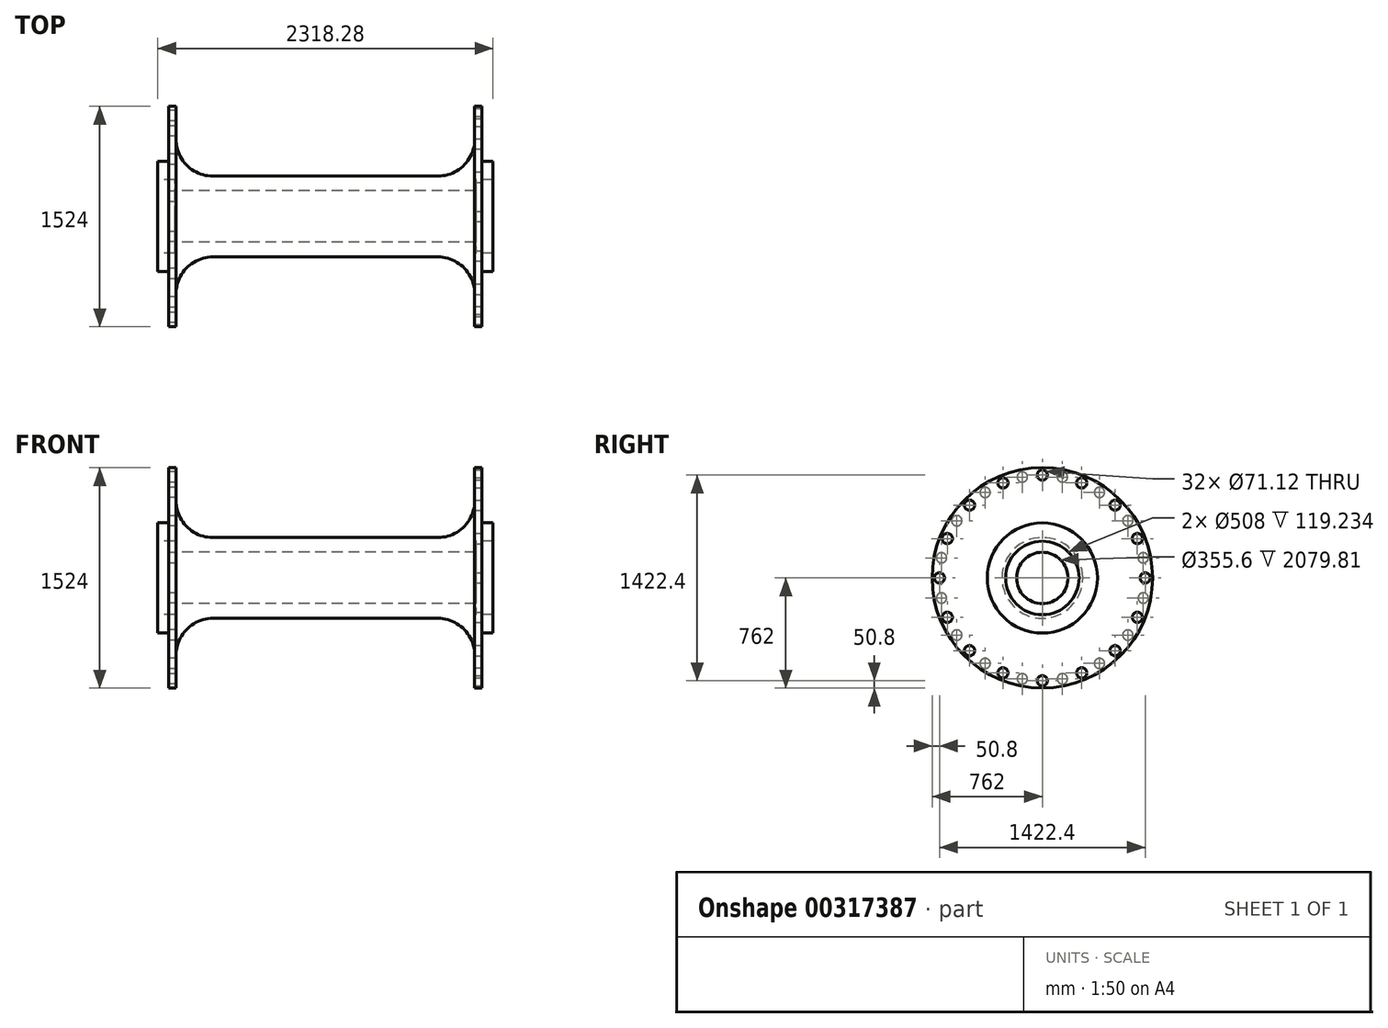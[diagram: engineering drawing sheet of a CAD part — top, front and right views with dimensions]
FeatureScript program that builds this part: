
annotation { "Feature Type Name" : "Feature", "Feature Type Description" : "" }
export const myFeature = defineFeature(function(context is Context, id is Id, definition is map)
    precondition{}
    {
        {
            var Q0;
            Q0=qCreatedBy(makeId("Front.planeOp"),FACE);
            var sketch = newSketch(context, id + "F0", { "sketchPlane" : qUnion([Q0])});
            skLineSegment(sketch, "E0", {"start": v(-1159.14, 0) * mm, "end": v(1380.86, 0) * mm});
            skLineSegment(sketch, "E1", {"start": v(-1159.14, 254) * mm, "end": v(-1039.9, 254) * mm});
            skLineSegment(sketch, "E2", {"start": v(-1039.9, 254) * mm, "end": v(-1039.9, 177.8) * mm});
            skLineSegment(sketch, "E3", {"start": v(-1039.9, 177.8) * mm, "end": v(0, 177.8) * mm});
            skLineSegment(sketch, "E4", {"start": v(0, 177.8) * mm, "end": v(0, 0) * mm});
            skLineSegment(sketch, "E5", {"start": v(-1159.14, 254) * mm, "end": v(-1159.14, 381) * mm});
            skLineSegment(sketch, "E6", {"start": v(-1159.14, 381) * mm, "end": v(-1082.94, 381) * mm});
            skLineSegment(sketch, "E7", {"start": v(-1082.94, 381) * mm, "end": v(-1082.94, 762) * mm});
            skLineSegment(sketch, "E8", {"start": v(-1082.94, 762) * mm, "end": v(-1032.14, 762) * mm});
            skLineSegment(sketch, "E9", {"start": v(-1032.14, 762) * mm, "end": v(-1032.14, 533.4) * mm});
            skLineSegment(sketch, "E10", {"start": v(0, 279.4) * mm, "end": v(-778.14, 279.4) * mm});
            skPoint(sketch, "E11.visualSharp", {"position": v(-1032.14, 279.4) * mm});
            skArc(sketch, "E11.filletArc", {"start": v(-1032.14, 533.4) * mm, "mid": v(-957.75, 353.8) * mm, "end": v(-778.14, 279.4) * mm});
            skLineSegment(sketch, "E12.MirrorCS", {"start": v(1159.14, 254) * mm, "end": v(1039.9, 254) * mm});
            skPoint(sketch, "E13.MirrorP", {"position": v(1032.14, 279.4) * mm});
            skLineSegment(sketch, "E14.MirrorCS", {"start": v(1039.9, 254) * mm, "end": v(1039.9, 177.8) * mm});
            skArc(sketch, "E15.MirrorCS", {"start": v(1032.14, 533.4) * mm, "mid": v(957.75, 353.8) * mm, "end": v(778.14, 279.4) * mm});
            skLineSegment(sketch, "E16.MirrorCS", {"start": v(1039.9, 177.8) * mm, "end": v(0, 177.8) * mm});
            skLineSegment(sketch, "E17.MirrorCS", {"start": v(0, 279.4) * mm, "end": v(778.14, 279.4) * mm});
            skLineSegment(sketch, "E18.MirrorCS", {"start": v(1082.94, 381) * mm, "end": v(1082.94, 762) * mm});
            skLineSegment(sketch, "E19.MirrorCS", {"start": v(1159.14, 381) * mm, "end": v(1082.94, 381) * mm});
            skLineSegment(sketch, "E20.MirrorCS", {"start": v(1082.94, 762) * mm, "end": v(1032.14, 762) * mm});
            skLineSegment(sketch, "E21.MirrorCS", {"start": v(1159.14, 254) * mm, "end": v(1159.14, 381) * mm});
            skLineSegment(sketch, "E22.MirrorCS", {"start": v(1032.14, 762) * mm, "end": v(1032.14, 533.4) * mm});
            skSolve(sketch);
        }
        {
            var Q0;
            Q0=makeQuery(id+"F0.imprint","IMPRINT",FACE,{"disambiguationData":[TD([[makeQuery(id+"F0.imprint","IMPRINT",EDGE,{"derivedFrom":sQuery(id+"F0.wireOp",EDGE,"E1")}),1.0]])]});
            var Q1;
            Q1=sQuery(id+"F0.wireOp",EDGE,"E0");
            revolve(context, id + "F1", {"entities" : qUnion([Q0]), "axis" : qUnion([Q1]), "revolveType" : RevolveType.FULL});
        }
        {
            var Q0;
            Q0=makeQuery(id+"F1.opRevolve","SWEPT_FACE",FACE,{"disambiguationData":[OSD([sQuery(id+"F0.wireOp",EDGE,"E18.MirrorCS")])]});
            var sketch = newSketch(context, id + "F2", { "sketchPlane" : qUnion([Q0])});
            skCircle(sketch, "E23", {"center": v(0, 711.2) * mm, "radius": 35.56 * mm});
            skPoint(sketch, "E24.center", {"position": v(0, 0) * mm});
            skCircle(sketch, "E25.1.0", {"center": v(-272.16, 657.06) * mm, "radius": 35.56 * mm});
            skCircle(sketch, "E25.2.0", {"center": v(-502.9, 502.9) * mm, "radius": 35.56 * mm});
            skCircle(sketch, "E25.3.0", {"center": v(-657.06, 272.16) * mm, "radius": 35.56 * mm});
            skCircle(sketch, "E25.4.0", {"center": v(-711.2, 0) * mm, "radius": 35.56 * mm});
            skCircle(sketch, "E25.5.0", {"center": v(-657.06, -272.16) * mm, "radius": 35.56 * mm});
            skCircle(sketch, "E25.6.0", {"center": v(-502.9, -502.9) * mm, "radius": 35.56 * mm});
            skCircle(sketch, "E25.7.0", {"center": v(-272.16, -657.06) * mm, "radius": 35.56 * mm});
            skCircle(sketch, "E25.8.0", {"center": v(0, -711.2) * mm, "radius": 35.56 * mm});
            skCircle(sketch, "E25.9.0", {"center": v(272.16, -657.06) * mm, "radius": 35.56 * mm});
            skCircle(sketch, "E25.10.0", {"center": v(502.9, -502.9) * mm, "radius": 35.56 * mm});
            skCircle(sketch, "E25.11.0", {"center": v(657.06, -272.16) * mm, "radius": 35.56 * mm});
            skCircle(sketch, "E25.12.0", {"center": v(711.2, 0) * mm, "radius": 35.56 * mm});
            skCircle(sketch, "E25.13.0", {"center": v(657.06, 272.16) * mm, "radius": 35.56 * mm});
            skCircle(sketch, "E25.14.0", {"center": v(502.9, 502.9) * mm, "radius": 35.56 * mm});
            skCircle(sketch, "E25.15.0", {"center": v(272.16, 657.06) * mm, "radius": 35.56 * mm});
            skSolve(sketch);
        }
        {
            var Q0;
            Q0 = qSketchRegion(id + "F2", true);
            extrude(context, id + "F3", {"entities" : qUnion([Q0]), "operationType" : NewBodyOperationType.REMOVE, "oppositeDirection" : true, "depth" : 302.26 * mm});
        }
        {
            var Q0;
            Q0=makeQuery(id+"F1.opRevolve","SWEPT_FACE",FACE,{"disambiguationData":[OSD([sQuery(id+"F0.wireOp",EDGE,"E7")])]});
            var sketch = newSketch(context, id + "F4", { "sketchPlane" : qUnion([Q0])});
            skLineSegment(sketch, "E26", {"start": v(0, 0) * mm, "end": v(0, 762) * mm});
            skLineSegment(sketch, "E27", {"start": v(0, 0) * mm, "end": v(148.66, 747.36) * mm});
            skCircle(sketch, "E28", {"center": v(138.75, 697.53) * mm, "radius": 35.56 * mm});
            skCircle(sketch, "E29.1.0", {"center": v(-138.75, 697.53) * mm, "radius": 35.56 * mm});
            skCircle(sketch, "E29.2.0", {"center": v(-395.12, 591.34) * mm, "radius": 35.56 * mm});
            skCircle(sketch, "E29.3.0", {"center": v(-591.34, 395.12) * mm, "radius": 35.56 * mm});
            skCircle(sketch, "E29.4.0", {"center": v(-697.53, 138.75) * mm, "radius": 35.56 * mm});
            skCircle(sketch, "E29.5.0", {"center": v(-697.53, -138.75) * mm, "radius": 35.56 * mm});
            skCircle(sketch, "E29.6.0", {"center": v(-591.34, -395.12) * mm, "radius": 35.56 * mm});
            skCircle(sketch, "E29.7.0", {"center": v(-395.12, -591.34) * mm, "radius": 35.56 * mm});
            skCircle(sketch, "E29.8.0", {"center": v(-138.75, -697.53) * mm, "radius": 35.56 * mm});
            skCircle(sketch, "E29.9.0", {"center": v(138.75, -697.53) * mm, "radius": 35.56 * mm});
            skCircle(sketch, "E29.10.0", {"center": v(395.12, -591.34) * mm, "radius": 35.56 * mm});
            skCircle(sketch, "E29.11.0", {"center": v(591.34, -395.12) * mm, "radius": 35.56 * mm});
            skCircle(sketch, "E29.12.0", {"center": v(697.53, -138.75) * mm, "radius": 35.56 * mm});
            skCircle(sketch, "E29.13.0", {"center": v(697.53, 138.75) * mm, "radius": 35.56 * mm});
            skCircle(sketch, "E29.14.0", {"center": v(591.34, 395.12) * mm, "radius": 35.56 * mm});
            skCircle(sketch, "E29.15.0", {"center": v(395.12, 591.34) * mm, "radius": 35.56 * mm});
            skPoint(sketch, "E29.center", {"position": v(0, 0) * mm});
            skSolve(sketch);
        }
        {
            var Q0;
            Q0 = qSketchRegion(id + "F4", true);
            extrude(context, id + "F5", {"entities" : qUnion([Q0]), "operationType" : NewBodyOperationType.REMOVE, "oppositeDirection" : true, "depth" : 431.8 * mm});
        }
    });
